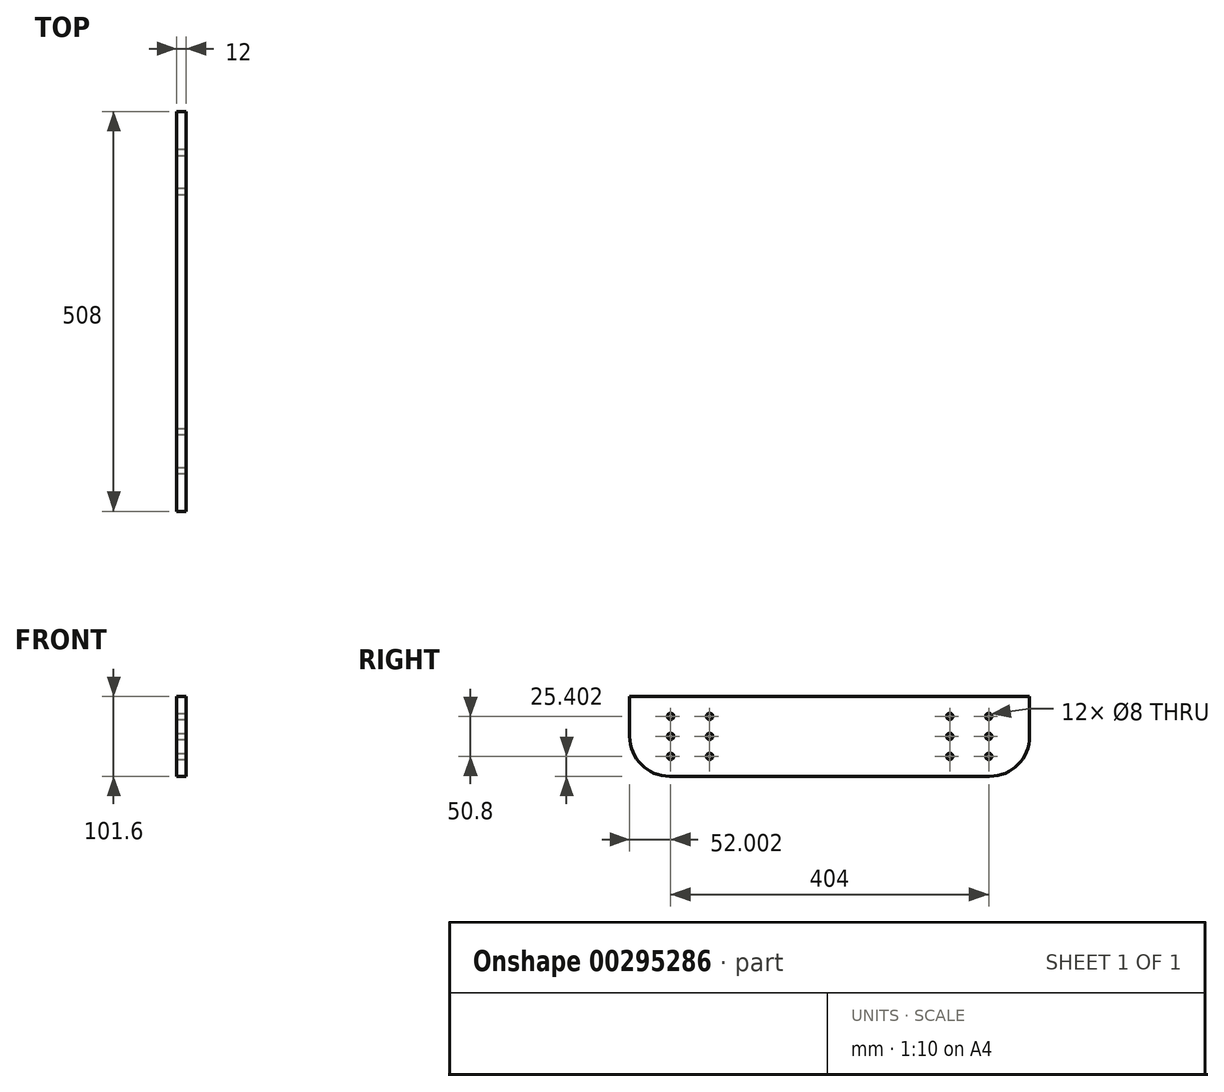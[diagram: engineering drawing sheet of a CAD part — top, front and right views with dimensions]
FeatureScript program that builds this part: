
annotation { "Feature Type Name" : "Feature", "Feature Type Description" : "" }
export const myFeature = defineFeature(function(context is Context, id is Id, definition is map)
    precondition{}
    {
        {
            var Q0;
            Q0=qCreatedBy(makeId("Right.planeOp"),FACE);
            var sketch = newSketch(context, id + "F0", { "sketchPlane" : qUnion([Q0])});
            skLineSegment(sketch, "E0.bottom", {"start": v(-246.07, 23.47) * mm, "end": v(261.93, 23.47) * mm});
            skLineSegment(sketch, "E0.top", {"start": v(-195.27, -78.13) * mm, "end": v(211.13, -78.13) * mm});
            skLineSegment(sketch, "E0.left", {"start": v(-246.07, 23.47) * mm, "end": v(-246.07, -27.33) * mm});
            skLineSegment(sketch, "E0.right", {"start": v(261.93, 23.47) * mm, "end": v(261.93, -27.33) * mm});
            skPoint(sketch, "E1.visualSharp", {"position": v(-246.07, -78.13) * mm});
            skArc(sketch, "E1.filletArc", {"start": v(-246.07, -27.33) * mm, "mid": v(-231.19, -63.25) * mm, "end": v(-195.27, -78.13) * mm});
            skPoint(sketch, "E2.visualSharp", {"position": v(261.93, -78.13) * mm});
            skArc(sketch, "E2.filletArc", {"start": v(211.13, -78.13) * mm, "mid": v(247.05, -63.25) * mm, "end": v(261.93, -27.33) * mm});
            skSolve(sketch);
        }
        {
            var Q0;
            Q0 = qSketchRegion(id + "F0", true);
            extrude(context, id + "F1", {"entities" : qUnion([Q0]), "depth" : 12 * mm});
        }
        {
            var Q0;
            Q0=makeQuery(id+"F1.opExtrude","CAP_FACE",FACE,{"disambiguationData":[OSD([sQuery(id+"F0.wireOp",EDGE,"E0.bottom"),sQuery(id+"F0.wireOp",EDGE,"E0.top"),sQuery(id+"F0.wireOp",EDGE,"E0.left"),sQuery(id+"F0.wireOp",EDGE,"E0.right"),sQuery(id+"F0.wireOp",EDGE,"E1.filletArc"),sQuery(id+"F0.wireOp",EDGE,"E2.filletArc")])],"isStart":false});
            var sketch = newSketch(context, id + "F2", { "sketchPlane" : qUnion([Q0])});
            skPoint(sketch, "E3", {"position": v(-144.57, -1.93) * mm});
            skPoint(sketch, "E4", {"position": v(-144.57, -27.33) * mm});
            skPoint(sketch, "E5", {"position": v(-144.57, -52.73) * mm});
            skPoint(sketch, "E6", {"position": v(-194.07, -52.73) * mm});
            skPoint(sketch, "E7", {"position": v(-194.07, -27.33) * mm});
            skPoint(sketch, "E8", {"position": v(-194.07, -1.93) * mm});
            skPoint(sketch, "E9", {"position": v(160.43, -1.93) * mm});
            skPoint(sketch, "E10", {"position": v(209.93, -1.93) * mm});
            skPoint(sketch, "E11", {"position": v(160.43, -27.33) * mm});
            skPoint(sketch, "E12", {"position": v(209.93, -27.33) * mm});
            skPoint(sketch, "E13", {"position": v(160.43, -52.73) * mm});
            skPoint(sketch, "E14", {"position": v(209.93, -52.73) * mm});
            skSolve(sketch);
        }
        {
            var Q0;
            Q0=sQuery(id+"F2.wireOp",VERTEX,"E8");
            var Q1;
            Q1=sQuery(id+"F2.wireOp",VERTEX,"E7");
            var Q2;
            Q2=sQuery(id+"F2.wireOp",VERTEX,"E6");
            var Q3;
            Q3=sQuery(id+"F2.wireOp",VERTEX,"E5");
            var Q4;
            Q4=sQuery(id+"F2.wireOp",VERTEX,"E4");
            var Q5;
            Q5=sQuery(id+"F2.wireOp",VERTEX,"E3");
            var Q6;
            Q6=sQuery(id+"F2.wireOp",VERTEX,"E9");
            var Q7;
            Q7=sQuery(id+"F2.wireOp",VERTEX,"E11");
            var Q8;
            Q8=sQuery(id+"F2.wireOp",VERTEX,"E13");
            var Q9;
            Q9=sQuery(id+"F2.wireOp",VERTEX,"E14");
            var Q10;
            Q10=sQuery(id+"F2.wireOp",VERTEX,"E12");
            var Q11;
            Q11=sQuery(id+"F2.wireOp",VERTEX,"E10");
            var Q12;
            Q12=makeQuery(id+"F1.opExtrude","SWEPT_BODY",BODY,{"disambiguationData":[OSD([sQuery(id+"F0.wireOp",EDGE,"E0.bottom"),sQuery(id+"F0.wireOp",EDGE,"E0.top"),sQuery(id+"F0.wireOp",EDGE,"E0.left"),sQuery(id+"F0.wireOp",EDGE,"E0.right"),sQuery(id+"F0.wireOp",EDGE,"E1.filletArc"),sQuery(id+"F0.wireOp",EDGE,"E2.filletArc")])]});
            hole(context, id + "F3", {"style" : HoleStyle.SIMPLE, "endStyle" : HoleEndStyle.THROUGH, "standardTappedOrClearance" : lookupTablePath({ "standard" : "ISO", "size" : "8", "type" : "Drilled" }), "standardBlindInLast" : lookupTablePath({ "standard" : "ISO", "size" : "8", "type" : "Drilled" }), "holeDiameter" : 8 * mm, "tappedDepth" : 12 * mm, "tapClearance" : 3, "locations" : qUnion([Q0, Q1, Q2, Q3, Q4, Q5, Q6, Q7, Q8, Q9, Q10, Q11]), "scope" : qUnion([Q12])});
        }
    });
